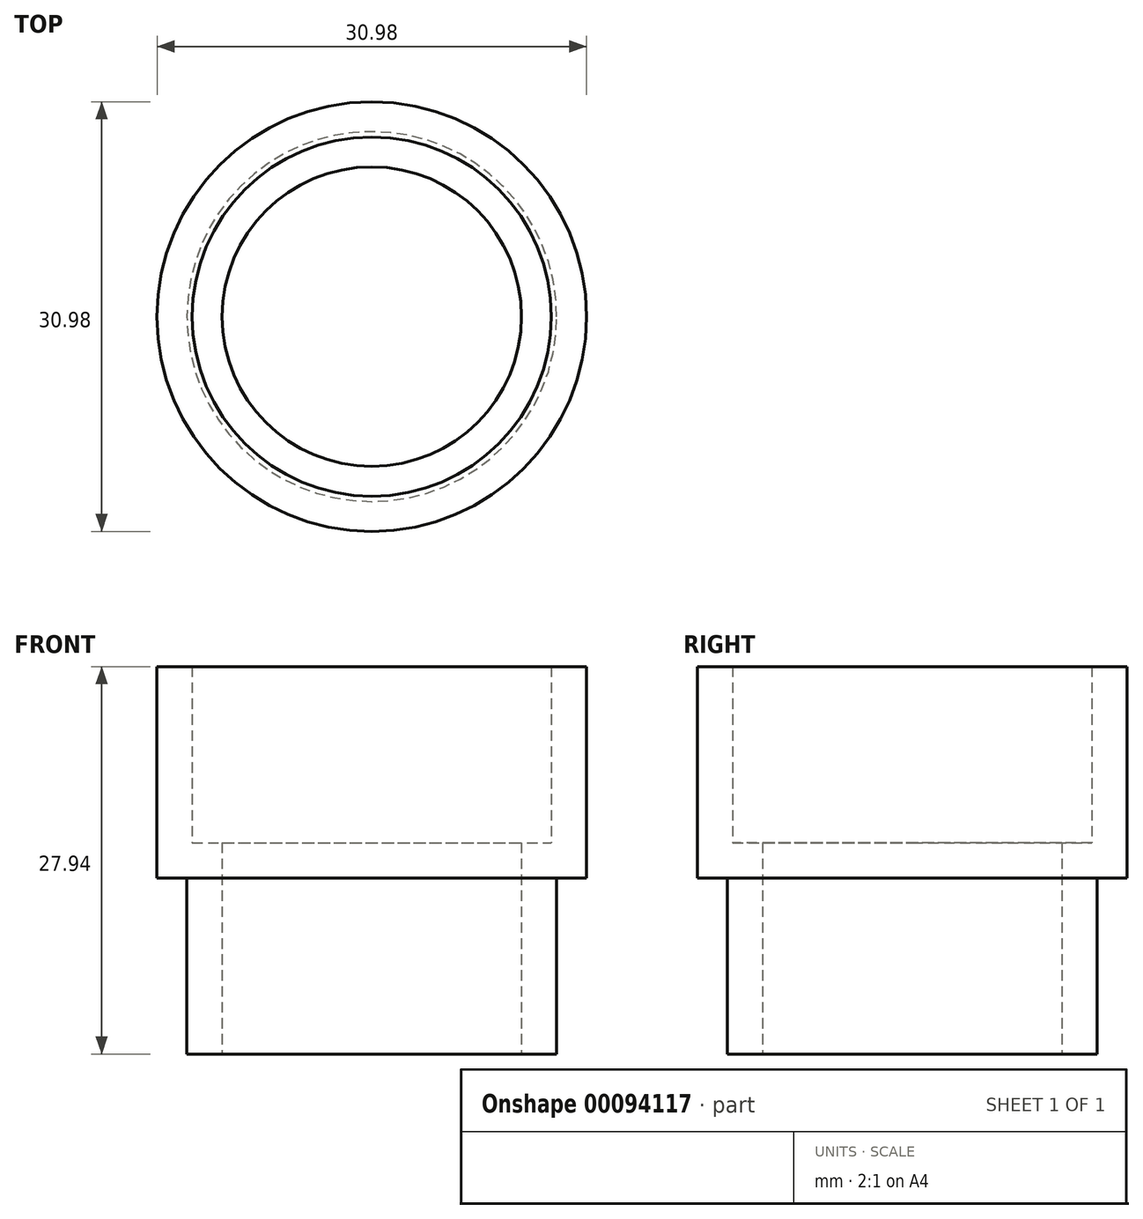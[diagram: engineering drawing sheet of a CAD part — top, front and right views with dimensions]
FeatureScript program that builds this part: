
annotation { "Feature Type Name" : "Feature", "Feature Type Description" : "" }
export const myFeature = defineFeature(function(context is Context, id is Id, definition is map)
    precondition{}
    {
        {
            var Q0;
            Q0=qCreatedBy(makeId("Front.planeOp"),FACE);
            var sketch = newSketch(context, id + "F0", { "sketchPlane" : qUnion([Q0])});
            skLineSegment(sketch, "E0", {"start": v(0, 0) * mm, "end": v(0, 25.78) * mm, "construction": true});
            skLineSegment(sketch, "E1.bottom", {"start": v(10.8, 0) * mm, "end": v(13.34, 0) * mm});
            skLineSegment(sketch, "E1.top", {"start": v(10.8, 12.7) * mm, "end": v(13.34, 12.7) * mm});
            skLineSegment(sketch, "E1.left", {"start": v(10.8, 0) * mm, "end": v(10.8, 12.7) * mm});
            skLineSegment(sketch, "E1.right", {"start": v(13.34, 0) * mm, "end": v(13.34, 12.7) * mm});
            skLineSegment(sketch, "E2.bottom", {"start": v(10.8, 12.7) * mm, "end": v(15.5, 12.7) * mm});
            skLineSegment(sketch, "E2.top", {"start": v(10.8, 15.24) * mm, "end": v(15.5, 15.24) * mm});
            skLineSegment(sketch, "E2.left", {"start": v(10.8, 12.7) * mm, "end": v(10.8, 15.24) * mm});
            skLineSegment(sketch, "E2.right", {"start": v(15.5, 12.7) * mm, "end": v(15.5, 15.24) * mm});
            skLineSegment(sketch, "E3", {"start": v(15.5, 15.24) * mm, "end": v(15.5, 27.94) * mm});
            skLineSegment(sketch, "E4", {"start": v(15.5, 27.94) * mm, "end": v(12.95, 27.94) * mm});
            skLineSegment(sketch, "E5", {"start": v(12.95, 27.94) * mm, "end": v(12.95, 15.24) * mm});
            skSolve(sketch);
        }
        {
            var Q0;
            {var subQ0=sQuery(id+"F0.wireOp",EDGE,"E3");Q0=makeQuery(id+"F0.imprint","IMPRINT",FACE,{"disambiguationData":[TD([[makeQuery(id+"F0.imprint","IMPRINT",EDGE,{"derivedFrom":subQ0}),1.0]])]});}
            var Q1;
            {var subQ3=sQuery(id+"F0.wireOp",EDGE,"E2.left");Q1=makeQuery(id+"F0.imprint","IMPRINT",FACE,{"disambiguationData":[TD([[makeQuery(id+"F0.imprint","IMPRINT",EDGE,{"derivedFrom":subQ3}),-1.0]])]});}
            var Q2;
            Q2=makeQuery(id+"F0.imprint","IMPRINT",FACE,{"disambiguationData":[TD([[makeQuery(id+"F0.imprint","IMPRINT",EDGE,{"derivedFrom":sQuery(id+"F0.wireOp",EDGE,"E1.bottom")}),1.0]])]});
            var Q3;
            Q3=sQuery(id+"F0.wireOp",EDGE,"E0");
            revolve(context, id + "F1", {"entities" : qUnion([Q0, Q1, Q2]), "axis" : qUnion([Q3]), "revolveType" : RevolveType.FULL});
        }
    });
